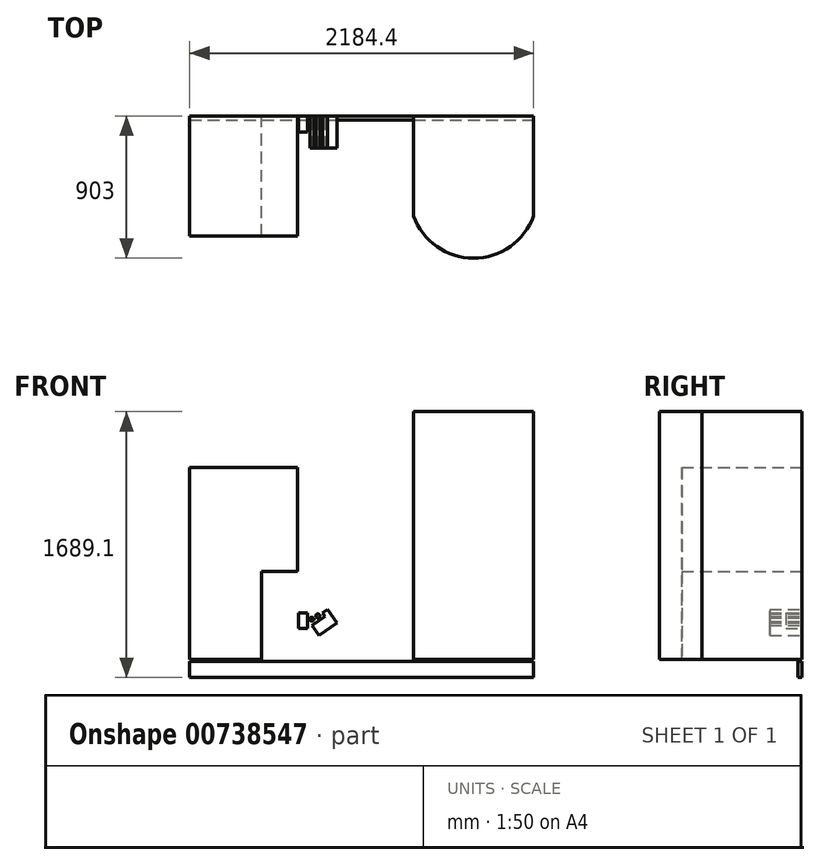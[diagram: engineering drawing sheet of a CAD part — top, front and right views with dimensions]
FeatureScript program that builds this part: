
annotation { "Feature Type Name" : "Feature", "Feature Type Description" : "" }
export const myFeature = defineFeature(function(context is Context, id is Id, definition is map)
    precondition{}
    {
        {
            var Q0;
            Q0=qCreatedBy(makeId("Front.planeOp"),FACE);
            var sketch = newSketch(context, id + "F0", { "sketchPlane" : qUnion([Q0])});
            skLineSegment(sketch, "E0", {"start": v(1225.78, -118) * mm, "end": v(-958.62, -118) * mm});
            skLineSegment(sketch, "E1", {"start": v(-958.62, -16.4) * mm, "end": v(1225.78, -16.4) * mm});
            skLineSegment(sketch, "E2", {"start": v(1225.78, -16.4) * mm, "end": v(1225.78, -118) * mm});
            skLineSegment(sketch, "E3", {"start": v(-958.62, -16.4) * mm, "end": v(-958.62, -118) * mm});
            skLineSegment(sketch, "E4.bottom", {"start": v(-958.62, -3.7) * mm, "end": v(-501.42, -3.7) * mm});
            skLineSegment(sketch, "E4.top", {"start": v(-958.62, 1215.5) * mm, "end": v(-501.42, 1215.5) * mm});
            skLineSegment(sketch, "E4.left", {"start": v(-958.62, -3.7) * mm, "end": v(-958.62, 1215.5) * mm});
            skLineSegment(sketch, "E5.bottom", {"start": v(463.78, -3.7) * mm, "end": v(1225.78, -3.7) * mm});
            skLineSegment(sketch, "E5.top", {"start": v(463.78, 1571.1) * mm, "end": v(1225.78, 1571.1) * mm});
            skLineSegment(sketch, "E5.left", {"start": v(463.78, -3.7) * mm, "end": v(463.78, 1571.1) * mm});
            skLineSegment(sketch, "E5.right", {"start": v(1225.78, -3.7) * mm, "end": v(1225.78, 1571.1) * mm});
            skLineSegment(sketch, "E6", {"start": v(-501.42, 1215.5) * mm, "end": v(-272.82, 1215.5) * mm});
            skLineSegment(sketch, "E7", {"start": v(-272.82, 1215.5) * mm, "end": v(-272.82, 555.1) * mm});
            skLineSegment(sketch, "E8", {"start": v(-272.82, 555.1) * mm, "end": v(-501.42, 555.1) * mm});
            skLineSegment(sketch, "E9", {"start": v(-501.42, 555.1) * mm, "end": v(-501.42, -3.7) * mm});
            skLineSegment(sketch, "E10", {"start": v(-138.33, 150.27) * mm, "end": v(-23.9, 230.4) * mm});
            skLineSegment(sketch, "E11", {"start": v(-23.9, 230.4) * mm, "end": v(-67.6, 292.82) * mm});
            skLineSegment(sketch, "E12", {"start": v(-67.6, 292.82) * mm, "end": v(-182.04, 212.7) * mm});
            skLineSegment(sketch, "E13", {"start": v(-182.04, 212.7) * mm, "end": v(-138.33, 150.27) * mm});
            skLineSegment(sketch, "E14", {"start": v(-67.6, 292.82) * mm, "end": v(-83.63, 315.71) * mm});
            skLineSegment(sketch, "E15", {"start": v(-83.63, 315.71) * mm, "end": v(-116.32, 292.82) * mm});
            skLineSegment(sketch, "E16", {"start": v(-116.32, 292.82) * mm, "end": v(-100.3, 269.93) * mm});
            skCircle(sketch, "E17", {"center": v(-182.04, 252.76) * mm, "radius": 12.7 * mm});
            skCircle(sketch, "E18", {"center": v(-144.93, 273.85) * mm, "radius": 12.7 * mm});
            skLineSegment(sketch, "E19.bottom", {"start": v(-267.3, 292.82) * mm, "end": v(-211.07, 292.82) * mm});
            skLineSegment(sketch, "E19.top", {"start": v(-267.3, 193.18) * mm, "end": v(-211.07, 193.18) * mm});
            skLineSegment(sketch, "E19.left", {"start": v(-267.3, 292.82) * mm, "end": v(-267.3, 193.18) * mm});
            skLineSegment(sketch, "E19.right", {"start": v(-211.07, 292.82) * mm, "end": v(-211.07, 193.18) * mm});
            skLineSegment(sketch, "E20.bottom", {"start": v(2123.86, -118) * mm, "end": v(-1974.62, -118) * mm});
            skLineSegment(sketch, "E20.top", {"start": v(2123.86, -1032.4) * mm, "end": v(-1974.62, -1032.4) * mm});
            skLineSegment(sketch, "E20.left", {"start": v(2123.86, -118) * mm, "end": v(2123.86, -1032.4) * mm});
            skLineSegment(sketch, "E20.right", {"start": v(-1974.62, -118) * mm, "end": v(-1974.62, -1032.4) * mm});
            skLineSegment(sketch, "E21.bottom", {"start": v(-958.62, 1723.33) * mm, "end": v(-1060.22, 1723.33) * mm});
            skLineSegment(sketch, "E21.top", {"start": v(-958.62, -118) * mm, "end": v(-1060.22, -118) * mm});
            skLineSegment(sketch, "E21.left", {"start": v(-958.62, 1723.33) * mm, "end": v(-958.62, -118) * mm});
            skLineSegment(sketch, "E21.right", {"start": v(-1060.22, 1723.33) * mm, "end": v(-1060.22, -118) * mm});
            skLineSegment(sketch, "E22.bottom", {"start": v(-1060.22, 2032.88) * mm, "end": v(-1974.62, 2032.88) * mm});
            skLineSegment(sketch, "E22.top", {"start": v(-1060.22, -1032.4) * mm, "end": v(-1974.62, -1032.4) * mm});
            skLineSegment(sketch, "E22.left", {"start": v(-1060.22, 2032.88) * mm, "end": v(-1060.22, -1032.4) * mm});
            skLineSegment(sketch, "E22.right", {"start": v(-1974.62, 2032.88) * mm, "end": v(-1974.62, -1032.4) * mm});
            skPoint(sketch, "E23", {"position": v(-124.82, 252.76) * mm});
            skSolve(sketch);
        }
        {
            var Q0;
            Q0=makeQuery(id+"F0.imprint","IMPRINT",FACE,{"disambiguationData":[TD([[makeQuery(id+"F0.imprint","IMPRINT",EDGE,{"derivedFrom":sQuery(id+"F0.wireOp",EDGE,"E4.bottom")}),1.0]])]});
            extrude(context, id + "F1", {"entities" : qUnion([Q0]), "depth" : 762 * mm, "offsetDistance" : 25.4 * mm});
        }
        {
            var Q0;
            Q0=makeQuery(id+"F0.imprint","IMPRINT",FACE,{"disambiguationData":[TD([[makeQuery(id+"F0.imprint","IMPRINT",EDGE,{"derivedFrom":sQuery(id+"F0.wireOp",EDGE,"E5.bottom")}),1.0]])]});
            extrude(context, id + "F2", {"entities" : qUnion([Q0]), "depth" : 635 * mm, "offsetDistance" : 25.4 * mm});
        }
        {
            var Q0;
            Q0=makeQuery(id+"F2.opExtrude","SWEPT_FACE",FACE,{"disambiguationData":[OSD([sQuery(id+"F0.wireOp",EDGE,"E5.bottom")])]});
            var sketch = newSketch(context, id + "F3", { "sketchPlane" : qUnion([Q0])});
            skArc(sketch, "E24", {"start": v(1225.78, 635) * mm, "mid": v(844.78, 903) * mm, "end": v(463.78, 635) * mm});
            skSolve(sketch);
        }
        {
            var Q0;
            Q0=makeQuery(id+"F3.imprint","IMPRINT",FACE,{"disambiguationData":[TD([[makeQuery(id+"F3.imprint","IMPRINT",EDGE,{"derivedFrom":sQuery(id+"F3.wireOp",EDGE,"E24")}),1.0]])]});
            extrude(context, id + "F4", {"entities" : qUnion([Q0]), "operationType" : NewBodyOperationType.ADD, "oppositeDirection" : true, "depth" : 1574.8 * mm, "offsetDistance" : 25.4 * mm});
        }
        {
            var Q0;
            Q0=makeQuery(id+"F0.imprint","IMPRINT",FACE,{"disambiguationData":[TD([[makeQuery(id+"F0.imprint","IMPRINT",EDGE,{"derivedFrom":sQuery(id+"F0.wireOp",EDGE,"E10")}),1.0]])]});
            var Q1;
            {var subQ0=sQuery(id+"F0.wireOp",EDGE,"E14");Q1=makeQuery(id+"F0.imprint","IMPRINT",FACE,{"disambiguationData":[TD([[makeQuery(id+"F0.imprint","IMPRINT",EDGE,{"derivedFrom":subQ0}),1.0]])]});}
            var Q2;
            Q2=makeQuery(id+"F0.imprint","IMPRINT",FACE,{"disambiguationData":[TD([[makeQuery(id+"F0.imprint","IMPRINT",EDGE,{"derivedFrom":sQuery(id+"F0.wireOp",EDGE,"E17")}),1.0]])]});
            var Q3;
            Q3=makeQuery(id+"F0.imprint","IMPRINT",FACE,{"disambiguationData":[TD([[makeQuery(id+"F0.imprint","IMPRINT",EDGE,{"derivedFrom":sQuery(id+"F0.wireOp",EDGE,"E18")}),1.0]])]});
            extrude(context, id + "F5", {"entities" : qUnion([Q0, Q1, Q2, Q3]), "depth" : 203.2 * mm, "offsetDistance" : 25.4 * mm});
        }
        {
            var Q0;
            Q0=makeQuery(id+"F0.imprint","IMPRINT",FACE,{"disambiguationData":[TD([[makeQuery(id+"F0.imprint","IMPRINT",EDGE,{"derivedFrom":sQuery(id+"F0.wireOp",EDGE,"E19.bottom")}),-1.0]])]});
            extrude(context, id + "F6", {"entities" : qUnion([Q0]), "depth" : 101.6 * mm, "offsetDistance" : 25.4 * mm});
        }
        {
            var Q0;
            {var subQ0=sQuery(id+"F0.wireOp",EDGE,"E1");Q0=makeQuery(id+"F0.imprint","IMPRINT",FACE,{"disambiguationData":[TD([[makeQuery(id+"F0.imprint","IMPRINT",EDGE,{"derivedFrom":subQ0}),-1.0]])]});}
            var Q1;
            {var subQ3=sQuery(id+"F0.wireOp",EDGE,"E21.bottom");Q1=makeQuery(id+"F0.imprint","IMPRINT",FACE,{"disambiguationData":[TD([[makeQuery(id+"F0.imprint","IMPRINT",EDGE,{"derivedFrom":subQ3}),1.0]])]});}
            extrude(context, id + "F7", {"entities" : qUnion([Q0, Q1]), "operationType" : NewBodyOperationType.ADD, "depth" : 25.4 * mm, "offsetDistance" : 25.4 * mm});
        }
    });
